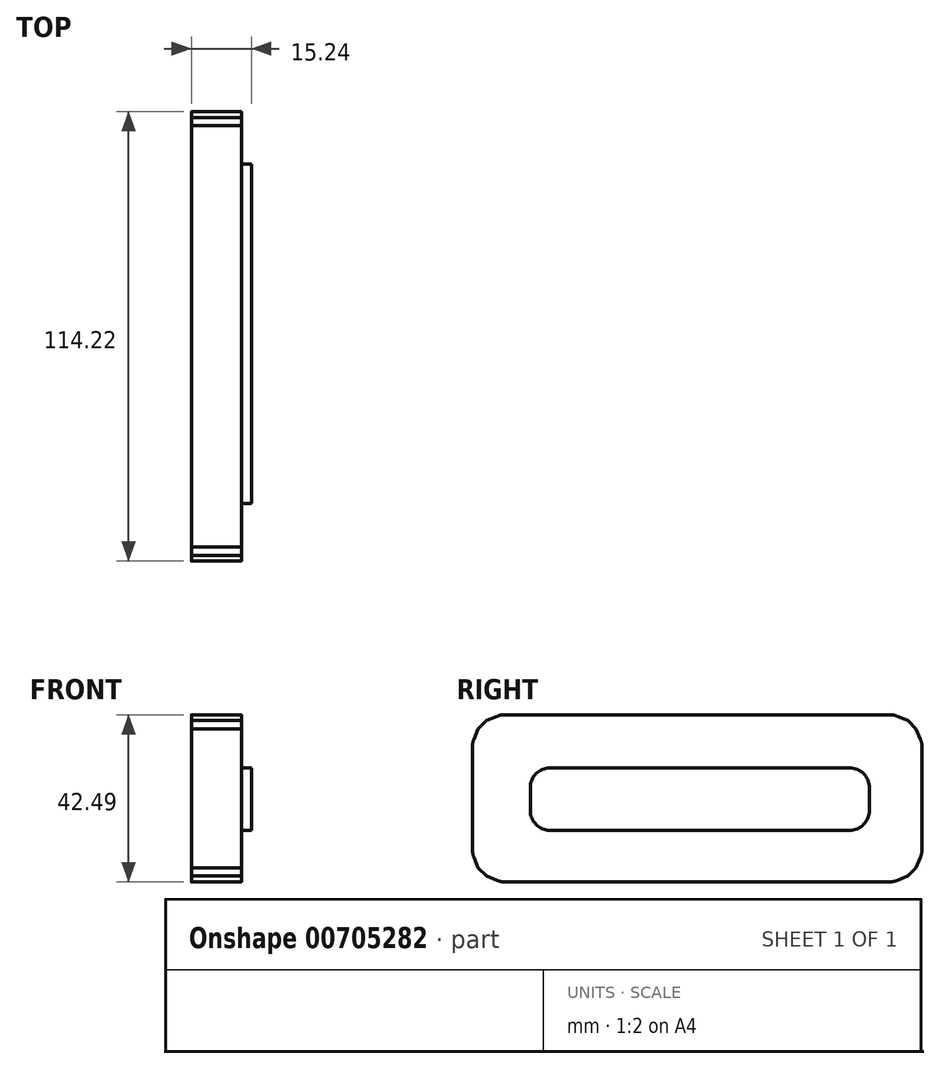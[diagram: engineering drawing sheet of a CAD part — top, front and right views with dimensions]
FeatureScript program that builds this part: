
annotation { "Feature Type Name" : "Feature", "Feature Type Description" : "" }
export const myFeature = defineFeature(function(context is Context, id is Id, definition is map)
    precondition{}
    {
        {
            var Q0;
            Q0=qCreatedBy(makeId("Right.planeOp"),FACE);
            var sketch = newSketch(context, id + "F0", { "sketchPlane" : qUnion([Q0])});
            skLineSegment(sketch, "E0.bottom", {"start": v(-46.33, 23.93) * mm, "end": v(67.9, 23.93) * mm});
            skLineSegment(sketch, "E0.top", {"start": v(-46.33, -18.56) * mm, "end": v(67.9, -18.56) * mm});
            skLineSegment(sketch, "E0.left", {"start": v(-46.33, 23.93) * mm, "end": v(-46.33, -18.56) * mm});
            skLineSegment(sketch, "E0.right", {"start": v(67.9, 23.93) * mm, "end": v(67.9, -18.56) * mm});
            skSolve(sketch);
        }
        {
            var Q0;
            Q0=qSketchRegion(id+"F0",true);
            extrude(context, id + "F1", {"entities" : qUnion([Q0]), "depth" : 12.7 * mm, "offsetDistance" : 25.4 * mm});
        }
        {
            var Q0;
            Q0=makeQuery(id+"F1.opExtrude","CAP_FACE",FACE,{"disambiguationData":[OSD([sQuery(id+"F0.wireOp",EDGE,"E0.bottom"),sQuery(id+"F0.wireOp",EDGE,"E0.top"),sQuery(id+"F0.wireOp",EDGE,"E0.left"),sQuery(id+"F0.wireOp",EDGE,"E0.right")])],"isStart":false});
            var sketch = newSketch(context, id + "F2", { "sketchPlane" : qUnion([Q0])});
            skLineSegment(sketch, "E1.bottom", {"start": v(-31.62, 10.44) * mm, "end": v(54.57, 10.44) * mm});
            skLineSegment(sketch, "E1.top", {"start": v(-31.62, -5.44) * mm, "end": v(54.57, -5.44) * mm});
            skLineSegment(sketch, "E1.left", {"start": v(-31.62, 10.44) * mm, "end": v(-31.62, -5.44) * mm});
            skLineSegment(sketch, "E1.right", {"start": v(54.57, 10.44) * mm, "end": v(54.57, -5.44) * mm});
            skSolve(sketch);
        }
        {
            var Q0;
            Q0 = qSketchRegion(id + "F2", true);
            extrude(context, id + "F3", {"entities" : qUnion([Q0]), "operationType" : NewBodyOperationType.ADD, "depth" : 2.54 * mm, "offsetDistance" : 25.4 * mm});
        }
        {
            var Q0;
            Q0=makeQuery(id+"F3.opExtrude","SWEPT_EDGE",EDGE,{"disambiguationData":[OSD([sQuery(id+"F2.wireOp",EDGE,"E1.bottom"),sQuery(id+"F2.wireOp",EDGE,"E1.left")])]});
            var Q1;
            Q1=makeQuery(id+"F3.opExtrude","SWEPT_EDGE",EDGE,{"disambiguationData":[OSD([sQuery(id+"F2.wireOp",EDGE,"E1.top"),sQuery(id+"F2.wireOp",EDGE,"E1.left")])]});
            var Q2;
            Q2=makeQuery(id+"F3.opExtrude","SWEPT_EDGE",EDGE,{"disambiguationData":[OSD([sQuery(id+"F2.wireOp",EDGE,"E1.bottom"),sQuery(id+"F2.wireOp",EDGE,"E1.right")])]});
            var Q3;
            Q3=makeQuery(id+"F3.opExtrude","SWEPT_EDGE",EDGE,{"disambiguationData":[OSD([sQuery(id+"F2.wireOp",EDGE,"E1.top"),sQuery(id+"F2.wireOp",EDGE,"E1.right")])]});
            fillet(context, id + "F4", {"entities" : qUnion([Q0, Q1, Q2, Q3]), "radius" : 5.08 * mm, "tangentPropagation" : true, "allowEdgeOverflow" : false});
        }
        {
            var Q0;
            Q0=makeQuery(id+"F1.opExtrude","SWEPT_EDGE",EDGE,{"disambiguationData":[OSD([sQuery(id+"F0.wireOp",EDGE,"E0.bottom"),sQuery(id+"F0.wireOp",EDGE,"E0.right")])]});
            var Q1;
            Q1=makeQuery(id+"F1.opExtrude","SWEPT_EDGE",EDGE,{"disambiguationData":[OSD([sQuery(id+"F0.wireOp",EDGE,"E0.top"),sQuery(id+"F0.wireOp",EDGE,"E0.right")])]});
            var Q2;
            Q2=makeQuery(id+"F1.opExtrude","SWEPT_EDGE",EDGE,{"disambiguationData":[OSD([sQuery(id+"F0.wireOp",EDGE,"E0.top"),sQuery(id+"F0.wireOp",EDGE,"E0.left")])]});
            var Q3;
            Q3=makeQuery(id+"F1.opExtrude","SWEPT_EDGE",EDGE,{"disambiguationData":[OSD([sQuery(id+"F0.wireOp",EDGE,"E0.bottom"),sQuery(id+"F0.wireOp",EDGE,"E0.left")])]});
            chamfer(context, id + "F5", {"entities" : qUnion([Q0, Q1, Q2, Q3]), "width" : 5.08 * mm, "tangentPropagation" : true});
        }
        {
            var Q0;
            {var subQ0=sQuery(id+"F0.wireOp",EDGE,"E0.left");Q0=makeQuery(id+"F5.opChamfer","BLEND_EDGE",EDGE,{"blendedFrom":[makeQuery(id+"F1.opExtrude","SWEPT_EDGE",EDGE,{"disambiguationData":[OSD([sQuery(id+"F0.wireOp",EDGE,"E0.bottom"),subQ0])]}),makeQuery(id+"F1.opExtrude","SWEPT_FACE",FACE,{"disambiguationData":[OSD([subQ0])]})],"blendedInto":[makeQuery(id+"F1.opExtrude","SWEPT_FACE",FACE,{"disambiguationData":[OSD([subQ0])]})]});}
            var Q1;
            {var subQ0=sQuery(id+"F0.wireOp",EDGE,"E0.bottom");Q1=makeQuery(id+"F5.opChamfer","BLEND_EDGE",EDGE,{"blendedFrom":[makeQuery(id+"F1.opExtrude","SWEPT_EDGE",EDGE,{"disambiguationData":[OSD([subQ0,sQuery(id+"F0.wireOp",EDGE,"E0.left")])]}),makeQuery(id+"F1.opExtrude","SWEPT_FACE",FACE,{"disambiguationData":[OSD([subQ0])]})],"blendedInto":[makeQuery(id+"F1.opExtrude","SWEPT_FACE",FACE,{"disambiguationData":[OSD([subQ0])]})]});}
            var Q2;
            {var subQ0=sQuery(id+"F0.wireOp",EDGE,"E0.bottom");Q2=makeQuery(id+"F5.opChamfer","BLEND_EDGE",EDGE,{"blendedFrom":[makeQuery(id+"F1.opExtrude","SWEPT_EDGE",EDGE,{"disambiguationData":[OSD([subQ0,sQuery(id+"F0.wireOp",EDGE,"E0.right")])]}),makeQuery(id+"F1.opExtrude","SWEPT_FACE",FACE,{"disambiguationData":[OSD([subQ0])]})],"blendedInto":[makeQuery(id+"F1.opExtrude","SWEPT_FACE",FACE,{"disambiguationData":[OSD([subQ0])]})]});}
            var Q3;
            {var subQ0=sQuery(id+"F0.wireOp",EDGE,"E0.right");Q3=makeQuery(id+"F5.opChamfer","BLEND_EDGE",EDGE,{"blendedFrom":[makeQuery(id+"F1.opExtrude","SWEPT_EDGE",EDGE,{"disambiguationData":[OSD([sQuery(id+"F0.wireOp",EDGE,"E0.bottom"),subQ0])]}),makeQuery(id+"F1.opExtrude","SWEPT_FACE",FACE,{"disambiguationData":[OSD([subQ0])]})],"blendedInto":[makeQuery(id+"F1.opExtrude","SWEPT_FACE",FACE,{"disambiguationData":[OSD([subQ0])]})]});}
            var Q4;
            {var subQ0=sQuery(id+"F0.wireOp",EDGE,"E0.right");Q4=makeQuery(id+"F5.opChamfer","BLEND_EDGE",EDGE,{"blendedFrom":[makeQuery(id+"F1.opExtrude","SWEPT_EDGE",EDGE,{"disambiguationData":[OSD([sQuery(id+"F0.wireOp",EDGE,"E0.top"),subQ0])]}),makeQuery(id+"F1.opExtrude","SWEPT_FACE",FACE,{"disambiguationData":[OSD([subQ0])]})],"blendedInto":[makeQuery(id+"F1.opExtrude","SWEPT_FACE",FACE,{"disambiguationData":[OSD([subQ0])]})]});}
            var Q5;
            {var subQ0=sQuery(id+"F0.wireOp",EDGE,"E0.top");Q5=makeQuery(id+"F5.opChamfer","BLEND_EDGE",EDGE,{"blendedFrom":[makeQuery(id+"F1.opExtrude","SWEPT_EDGE",EDGE,{"disambiguationData":[OSD([subQ0,sQuery(id+"F0.wireOp",EDGE,"E0.right")])]}),makeQuery(id+"F1.opExtrude","SWEPT_FACE",FACE,{"disambiguationData":[OSD([subQ0])]})],"blendedInto":[makeQuery(id+"F1.opExtrude","SWEPT_FACE",FACE,{"disambiguationData":[OSD([subQ0])]})]});}
            var Q6;
            {var subQ0=sQuery(id+"F0.wireOp",EDGE,"E0.left");Q6=makeQuery(id+"F5.opChamfer","BLEND_EDGE",EDGE,{"blendedFrom":[makeQuery(id+"F1.opExtrude","SWEPT_EDGE",EDGE,{"disambiguationData":[OSD([sQuery(id+"F0.wireOp",EDGE,"E0.top"),subQ0])]}),makeQuery(id+"F1.opExtrude","SWEPT_FACE",FACE,{"disambiguationData":[OSD([subQ0])]})],"blendedInto":[makeQuery(id+"F1.opExtrude","SWEPT_FACE",FACE,{"disambiguationData":[OSD([subQ0])]})]});}
            var Q7;
            {var subQ0=sQuery(id+"F0.wireOp",EDGE,"E0.top");Q7=makeQuery(id+"F5.opChamfer","BLEND_EDGE",EDGE,{"blendedFrom":[makeQuery(id+"F1.opExtrude","SWEPT_EDGE",EDGE,{"disambiguationData":[OSD([subQ0,sQuery(id+"F0.wireOp",EDGE,"E0.left")])]}),makeQuery(id+"F1.opExtrude","SWEPT_FACE",FACE,{"disambiguationData":[OSD([subQ0])]})],"blendedInto":[makeQuery(id+"F1.opExtrude","SWEPT_FACE",FACE,{"disambiguationData":[OSD([subQ0])]})]});}
            chamfer(context, id + "F6", {"entities" : qUnion([Q0, Q1, Q2, Q3, Q4, Q5, Q6, Q7]), "width" : 5.08 * mm, "tangentPropagation" : true});
        }
        {
            var Q0;
            {var subQ0=sQuery(id+"F0.wireOp",EDGE,"E0.left");var subQ1=sQuery(id+"F0.wireOp",EDGE,"E0.top");var subQ2=makeQuery(id+"F1.opExtrude","SWEPT_EDGE",EDGE,{"disambiguationData":[OSD([subQ1,subQ0])]});Q0=makeQuery(id+"F6.opChamfer","BLEND_EDGE",EDGE,{"blendedFrom":[makeQuery(id+"F5.opChamfer","BLEND_EDGE",EDGE,{"blendedFrom":[subQ2,makeQuery(id+"F1.opExtrude","SWEPT_FACE",FACE,{"disambiguationData":[OSD([subQ1])]})],"blendedInto":[makeQuery(id+"F1.opExtrude","SWEPT_FACE",FACE,{"disambiguationData":[OSD([subQ1])]})]}),makeQuery(id+"F5.opChamfer","BLEND_EDGE",EDGE,{"blendedFrom":[subQ2,makeQuery(id+"F1.opExtrude","SWEPT_FACE",FACE,{"disambiguationData":[OSD([subQ0])]})],"blendedInto":[makeQuery(id+"F1.opExtrude","SWEPT_FACE",FACE,{"disambiguationData":[OSD([subQ0])]})]})],"blendedInto":[]});}
            var Q1;
            {var subQ0=sQuery(id+"F0.wireOp",EDGE,"E0.top");var subQ1=makeQuery(id+"F1.opExtrude","SWEPT_FACE",FACE,{"disambiguationData":[OSD([subQ0])]});Q1=makeQuery(id+"F6.opChamfer","BLEND_EDGE",EDGE,{"blendedFrom":[makeQuery(id+"F5.opChamfer","BLEND_EDGE",EDGE,{"blendedFrom":[makeQuery(id+"F1.opExtrude","SWEPT_EDGE",EDGE,{"disambiguationData":[OSD([subQ0,sQuery(id+"F0.wireOp",EDGE,"E0.left")])]}),subQ1],"blendedInto":[subQ1]}),subQ1],"blendedInto":[subQ1]});}
            var Q2;
            {var subQ0=sQuery(id+"F0.wireOp",EDGE,"E0.left");var subQ1=makeQuery(id+"F1.opExtrude","SWEPT_FACE",FACE,{"disambiguationData":[OSD([subQ0])]});Q2=makeQuery(id+"F6.opChamfer","BLEND_EDGE",EDGE,{"blendedFrom":[makeQuery(id+"F5.opChamfer","BLEND_EDGE",EDGE,{"blendedFrom":[makeQuery(id+"F1.opExtrude","SWEPT_EDGE",EDGE,{"disambiguationData":[OSD([sQuery(id+"F0.wireOp",EDGE,"E0.top"),subQ0])]}),subQ1],"blendedInto":[subQ1]}),subQ1],"blendedInto":[subQ1]});}
            var Q3;
            {var subQ0=sQuery(id+"F0.wireOp",EDGE,"E0.left");var subQ1=sQuery(id+"F0.wireOp",EDGE,"E0.bottom");var subQ2=makeQuery(id+"F1.opExtrude","SWEPT_EDGE",EDGE,{"disambiguationData":[OSD([subQ1,subQ0])]});Q3=makeQuery(id+"F6.opChamfer","BLEND_EDGE",EDGE,{"blendedFrom":[makeQuery(id+"F5.opChamfer","BLEND_EDGE",EDGE,{"blendedFrom":[subQ2,makeQuery(id+"F1.opExtrude","SWEPT_FACE",FACE,{"disambiguationData":[OSD([subQ1])]})],"blendedInto":[makeQuery(id+"F1.opExtrude","SWEPT_FACE",FACE,{"disambiguationData":[OSD([subQ1])]})]}),makeQuery(id+"F5.opChamfer","BLEND_EDGE",EDGE,{"blendedFrom":[subQ2,makeQuery(id+"F1.opExtrude","SWEPT_FACE",FACE,{"disambiguationData":[OSD([subQ0])]})],"blendedInto":[makeQuery(id+"F1.opExtrude","SWEPT_FACE",FACE,{"disambiguationData":[OSD([subQ0])]})]})],"blendedInto":[]});}
            var Q4;
            {var subQ0=sQuery(id+"F0.wireOp",EDGE,"E0.left");var subQ1=makeQuery(id+"F1.opExtrude","SWEPT_FACE",FACE,{"disambiguationData":[OSD([subQ0])]});Q4=makeQuery(id+"F6.opChamfer","BLEND_EDGE",EDGE,{"blendedFrom":[makeQuery(id+"F5.opChamfer","BLEND_EDGE",EDGE,{"blendedFrom":[makeQuery(id+"F1.opExtrude","SWEPT_EDGE",EDGE,{"disambiguationData":[OSD([sQuery(id+"F0.wireOp",EDGE,"E0.bottom"),subQ0])]}),subQ1],"blendedInto":[subQ1]}),subQ1],"blendedInto":[subQ1]});}
            var Q5;
            {var subQ0=sQuery(id+"F0.wireOp",EDGE,"E0.bottom");var subQ1=makeQuery(id+"F1.opExtrude","SWEPT_FACE",FACE,{"disambiguationData":[OSD([subQ0])]});Q5=makeQuery(id+"F6.opChamfer","BLEND_EDGE",EDGE,{"blendedFrom":[makeQuery(id+"F5.opChamfer","BLEND_EDGE",EDGE,{"blendedFrom":[makeQuery(id+"F1.opExtrude","SWEPT_EDGE",EDGE,{"disambiguationData":[OSD([subQ0,sQuery(id+"F0.wireOp",EDGE,"E0.left")])]}),subQ1],"blendedInto":[subQ1]}),subQ1],"blendedInto":[subQ1]});}
            var Q6;
            {var subQ0=sQuery(id+"F0.wireOp",EDGE,"E0.bottom");var subQ1=makeQuery(id+"F1.opExtrude","SWEPT_FACE",FACE,{"disambiguationData":[OSD([subQ0])]});Q6=makeQuery(id+"F6.opChamfer","BLEND_EDGE",EDGE,{"blendedFrom":[makeQuery(id+"F5.opChamfer","BLEND_EDGE",EDGE,{"blendedFrom":[makeQuery(id+"F1.opExtrude","SWEPT_EDGE",EDGE,{"disambiguationData":[OSD([subQ0,sQuery(id+"F0.wireOp",EDGE,"E0.right")])]}),subQ1],"blendedInto":[subQ1]}),subQ1],"blendedInto":[subQ1]});}
            var Q7;
            {var subQ0=sQuery(id+"F0.wireOp",EDGE,"E0.right");var subQ1=sQuery(id+"F0.wireOp",EDGE,"E0.bottom");var subQ2=makeQuery(id+"F1.opExtrude","SWEPT_EDGE",EDGE,{"disambiguationData":[OSD([subQ1,subQ0])]});Q7=makeQuery(id+"F6.opChamfer","BLEND_EDGE",EDGE,{"blendedFrom":[makeQuery(id+"F5.opChamfer","BLEND_EDGE",EDGE,{"blendedFrom":[subQ2,makeQuery(id+"F1.opExtrude","SWEPT_FACE",FACE,{"disambiguationData":[OSD([subQ1])]})],"blendedInto":[makeQuery(id+"F1.opExtrude","SWEPT_FACE",FACE,{"disambiguationData":[OSD([subQ1])]})]}),makeQuery(id+"F5.opChamfer","BLEND_EDGE",EDGE,{"blendedFrom":[subQ2,makeQuery(id+"F1.opExtrude","SWEPT_FACE",FACE,{"disambiguationData":[OSD([subQ0])]})],"blendedInto":[makeQuery(id+"F1.opExtrude","SWEPT_FACE",FACE,{"disambiguationData":[OSD([subQ0])]})]})],"blendedInto":[]});}
            var Q8;
            {var subQ0=sQuery(id+"F0.wireOp",EDGE,"E0.right");var subQ1=makeQuery(id+"F1.opExtrude","SWEPT_FACE",FACE,{"disambiguationData":[OSD([subQ0])]});Q8=makeQuery(id+"F6.opChamfer","BLEND_EDGE",EDGE,{"blendedFrom":[makeQuery(id+"F5.opChamfer","BLEND_EDGE",EDGE,{"blendedFrom":[makeQuery(id+"F1.opExtrude","SWEPT_EDGE",EDGE,{"disambiguationData":[OSD([sQuery(id+"F0.wireOp",EDGE,"E0.bottom"),subQ0])]}),subQ1],"blendedInto":[subQ1]}),subQ1],"blendedInto":[subQ1]});}
            var Q9;
            {var subQ0=sQuery(id+"F0.wireOp",EDGE,"E0.right");var subQ1=makeQuery(id+"F1.opExtrude","SWEPT_FACE",FACE,{"disambiguationData":[OSD([subQ0])]});Q9=makeQuery(id+"F6.opChamfer","BLEND_EDGE",EDGE,{"blendedFrom":[makeQuery(id+"F5.opChamfer","BLEND_EDGE",EDGE,{"blendedFrom":[makeQuery(id+"F1.opExtrude","SWEPT_EDGE",EDGE,{"disambiguationData":[OSD([sQuery(id+"F0.wireOp",EDGE,"E0.top"),subQ0])]}),subQ1],"blendedInto":[subQ1]}),subQ1],"blendedInto":[subQ1]});}
            var Q10;
            {var subQ0=sQuery(id+"F0.wireOp",EDGE,"E0.right");var subQ1=sQuery(id+"F0.wireOp",EDGE,"E0.top");var subQ2=makeQuery(id+"F1.opExtrude","SWEPT_EDGE",EDGE,{"disambiguationData":[OSD([subQ1,subQ0])]});Q10=makeQuery(id+"F6.opChamfer","BLEND_EDGE",EDGE,{"blendedFrom":[makeQuery(id+"F5.opChamfer","BLEND_EDGE",EDGE,{"blendedFrom":[subQ2,makeQuery(id+"F1.opExtrude","SWEPT_FACE",FACE,{"disambiguationData":[OSD([subQ1])]})],"blendedInto":[makeQuery(id+"F1.opExtrude","SWEPT_FACE",FACE,{"disambiguationData":[OSD([subQ1])]})]}),makeQuery(id+"F5.opChamfer","BLEND_EDGE",EDGE,{"blendedFrom":[subQ2,makeQuery(id+"F1.opExtrude","SWEPT_FACE",FACE,{"disambiguationData":[OSD([subQ0])]})],"blendedInto":[makeQuery(id+"F1.opExtrude","SWEPT_FACE",FACE,{"disambiguationData":[OSD([subQ0])]})]})],"blendedInto":[]});}
            var Q11;
            {var subQ0=sQuery(id+"F0.wireOp",EDGE,"E0.top");var subQ1=makeQuery(id+"F1.opExtrude","SWEPT_FACE",FACE,{"disambiguationData":[OSD([subQ0])]});Q11=makeQuery(id+"F6.opChamfer","BLEND_EDGE",EDGE,{"blendedFrom":[makeQuery(id+"F5.opChamfer","BLEND_EDGE",EDGE,{"blendedFrom":[makeQuery(id+"F1.opExtrude","SWEPT_EDGE",EDGE,{"disambiguationData":[OSD([subQ0,sQuery(id+"F0.wireOp",EDGE,"E0.right")])]}),subQ1],"blendedInto":[subQ1]}),subQ1],"blendedInto":[subQ1]});}
            fillet(context, id + "F7", {"entities" : qUnion([Q0, Q1, Q2, Q3, Q4, Q5, Q6, Q7, Q8, Q9, Q10, Q11]), "radius" : 5.08 * mm, "tangentPropagation" : true, "allowEdgeOverflow" : false});
        }
    });
